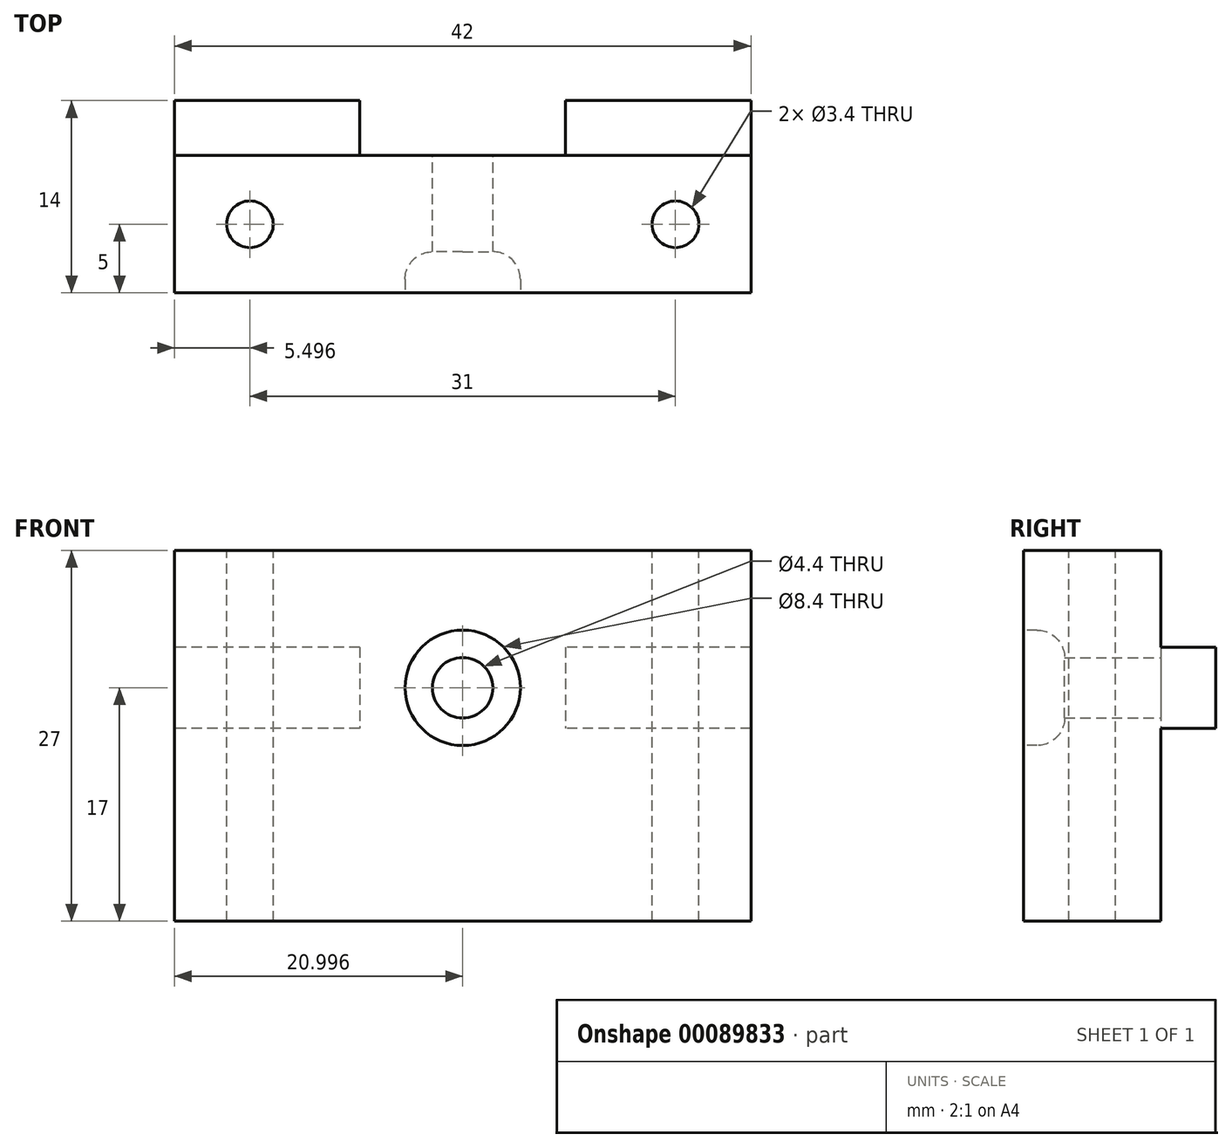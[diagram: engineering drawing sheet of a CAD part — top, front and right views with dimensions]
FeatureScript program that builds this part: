
annotation { "Feature Type Name" : "Feature", "Feature Type Description" : "" }
export const myFeature = defineFeature(function(context is Context, id is Id, definition is map)
    precondition{}
    {
        {
            var Q0;
            Q0=qCreatedBy(makeId("Top.planeOp"),FACE);
            var sketch = newSketch(context, id + "F0", { "sketchPlane" : qUnion([Q0])});
            skLineSegment(sketch, "E0.bottom", {"start": v(-16.85, 0) * mm, "end": v(25.15, 0) * mm});
            skLineSegment(sketch, "E0.top", {"start": v(-16.85, 10) * mm, "end": v(25.15, 10) * mm});
            skLineSegment(sketch, "E0.left", {"start": v(-16.85, 0) * mm, "end": v(-16.85, 10) * mm});
            skLineSegment(sketch, "E0.right", {"start": v(25.15, 0) * mm, "end": v(25.15, 10) * mm});
            skSolve(sketch);
        }
        {
            var Q0;
            Q0=qSketchRegion(id+"F0",true);
            extrude(context, id + "F1", {"entities" : qUnion([Q0]), "depth" : 27 * mm});
        }
        {
            var Q0;
            Q0=makeQuery(id+"F1.opExtrude","CAP_FACE",FACE,{"disambiguationData":[OSD([sQuery(id+"F0.wireOp",EDGE,"E0.bottom"),sQuery(id+"F0.wireOp",EDGE,"E0.top"),sQuery(id+"F0.wireOp",EDGE,"E0.left"),sQuery(id+"F0.wireOp",EDGE,"E0.right")])],"isStart":false});
            var sketch = newSketch(context, id + "F2", { "sketchPlane" : qUnion([Q0])});
            skCircle(sketch, "E1", {"center": v(-11.35, 5) * mm, "radius": 1.7 * mm});
            skCircle(sketch, "E2", {"center": v(19.65, 5) * mm, "radius": 1.7 * mm});
            skPoint(sketch, "E3", {"position": v(-16.85, 5) * mm});
            skLineSegment(sketch, "E4", {"start": v(-11.35, 5) * mm, "end": v(-16.85, 5) * mm});
            skLineSegment(sketch, "E5", {"start": v(19.65, 5) * mm, "end": v(25.15, 5) * mm});
            skSolve(sketch);
        }
        {
            var Q0;
            Q0=qSketchRegion(id+"F2",true);
            extrude(context, id + "F3", {"entities" : qUnion([Q0]), "operationType" : NewBodyOperationType.REMOVE, "endBound" : BoundingType.THROUGH_ALL, "oppositeDirection" : true, "depth" : 25 * mm});
        }
        {
            var Q0;
            Q0=makeQuery(id+"F1.opExtrude","SWEPT_FACE",FACE,{"disambiguationData":[OSD([sQuery(id+"F0.wireOp",EDGE,"E0.top")])]});
            var sketch = newSketch(context, id + "F4", { "sketchPlane" : qUnion([Q0])});
            skLineSegment(sketch, "E6.bottom", {"start": v(-25.15, 14.05) * mm, "end": v(16.85, 14.05) * mm});
            skLineSegment(sketch, "E6.top", {"start": v(-25.15, 19.95) * mm, "end": v(16.85, 19.95) * mm});
            skLineSegment(sketch, "E6.left", {"start": v(-25.15, 14.05) * mm, "end": v(-25.15, 19.95) * mm});
            skLineSegment(sketch, "E6.right", {"start": v(16.85, 14.05) * mm, "end": v(16.85, 19.95) * mm});
            skLineSegment(sketch, "E7", {"start": v(-4.15, 19.95) * mm, "end": v(-4.15, 27) * mm});
            skLineSegment(sketch, "E8.bottom", {"start": v(-11.65, 19.95) * mm, "end": v(3.35, 19.95) * mm});
            skLineSegment(sketch, "E8.top", {"start": v(-11.65, 14.05) * mm, "end": v(3.35, 14.05) * mm});
            skLineSegment(sketch, "E8.left", {"start": v(-11.65, 19.95) * mm, "end": v(-11.65, 14.05) * mm});
            skLineSegment(sketch, "E8.right", {"start": v(3.35, 19.95) * mm, "end": v(3.35, 14.05) * mm});
            skPoint(sketch, "E9", {"position": v(-4.15, 19.95) * mm});
            skCircle(sketch, "E10", {"center": v(-4.15, 17) * mm, "radius": 2.2 * mm});
            skPoint(sketch, "E11", {"position": v(-11.65, 17) * mm});
            skSolve(sketch);
        }
        {
            var Q0;
            {var subQ0=sQuery(id+"F4.wireOp",EDGE,"E6.left");Q0=makeQuery(id+"F4.imprint","IMPRINT",FACE,{"disambiguationData":[TD([[makeQuery(id+"F4.imprint","IMPRINT",EDGE,{"derivedFrom":subQ0}),1.0]])]});}
            var Q1;
            {var subQ0=sQuery(id+"F4.wireOp",EDGE,"E6.right");Q1=makeQuery(id+"F4.imprint","IMPRINT",FACE,{"disambiguationData":[TD([[makeQuery(id+"F4.imprint","IMPRINT",EDGE,{"derivedFrom":subQ0}),-1.0]])]});}
            extrude(context, id + "F5", {"entities" : qUnion([Q0, Q1]), "operationType" : NewBodyOperationType.ADD, "depth" : 4 * mm});
        }
        {
            var Q0;
            Q0=makeQuery(id+"F4.imprint","IMPRINT",FACE,{"disambiguationData":[TD([[makeQuery(id+"F4.imprint","IMPRINT",EDGE,{"derivedFrom":sQuery(id+"F4.wireOp",EDGE,"E10")}),1.0]])]});
            extrude(context, id + "F6", {"entities" : qUnion([Q0]), "operationType" : NewBodyOperationType.REMOVE, "oppositeDirection" : true, "depth" : 25 * mm});
        }
        {
            var Q0;
            Q0=makeQuery(id+"F1.opExtrude","SWEPT_FACE",FACE,{"disambiguationData":[OSD([sQuery(id+"F0.wireOp",EDGE,"E0.bottom")])]});
            var sketch = newSketch(context, id + "F7", { "sketchPlane" : qUnion([Q0])});
            skCircle(sketch, "E12", {"center": v(4.15, 17) * mm, "radius": 4.2 * mm});
            skSolve(sketch);
        }
        {
            var Q0;
            Q0=qSketchRegion(id+"F7",true);
            extrude(context, id + "F8", {"entities" : qUnion([Q0]), "operationType" : NewBodyOperationType.REMOVE, "oppositeDirection" : true, "depth" : 3 * mm});
        }
        {
            var Q0;
            Q0=makeQuery(id+"F8.boolean.opBoolean","COPY",EDGE,{"derivedFrom":makeQuery(id+"F8.opExtrude","CAP_EDGE",EDGE,{"disambiguationData":[OSD([sQuery(id+"F7.wireOp",EDGE,"E12")])],"isStart":false})});
            fillet(context, id + "F9", {"entities" : qUnion([Q0]), "radius" : 2 * mm, "tangentPropagation" : true, "allowEdgeOverflow" : false});
        }
    });
